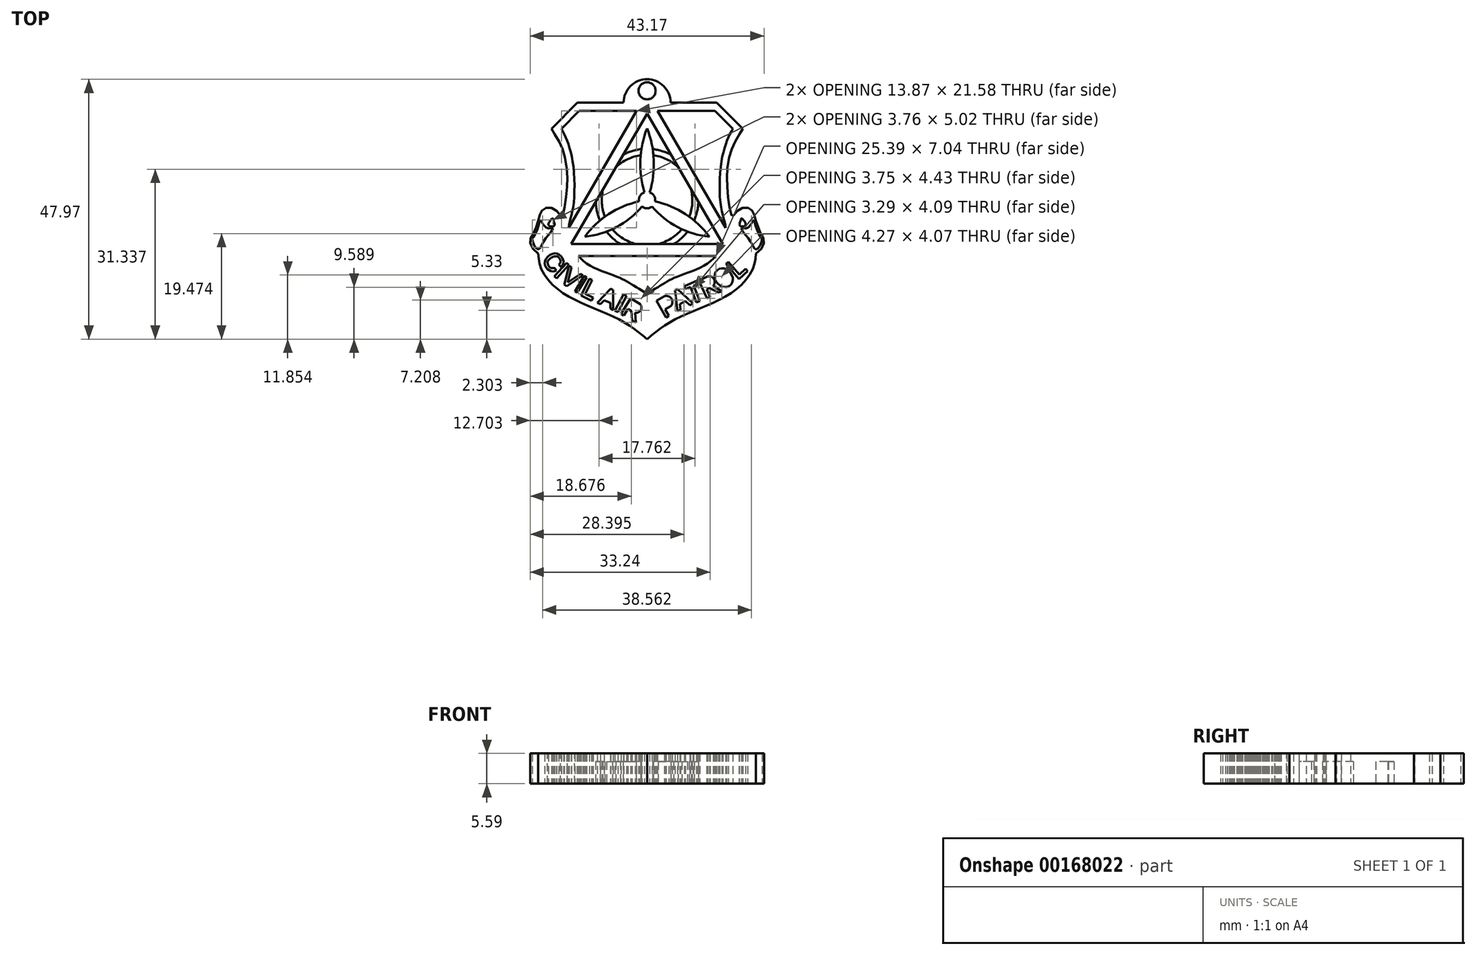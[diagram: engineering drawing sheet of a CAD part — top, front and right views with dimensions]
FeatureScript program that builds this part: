
annotation { "Feature Type Name" : "Feature", "Feature Type Description" : "" }
export const myFeature = defineFeature(function(context is Context, id is Id, definition is map)
    precondition{}
    {
        {
            var Q0;
            Q0=qCreatedBy(makeId("Top.planeOp"),FACE);
            var sketch = newSketch(context, id + "F0", { "sketchPlane" : qUnion([Q0])});
            skLineSegment(sketch, "E0", {"start": v(-6.93, 17.49) * mm, "end": v(-15.48, 17.49) * mm});
            skLineSegment(sketch, "E1", {"start": v(-15.48, 17.49) * mm, "end": v(-20.25, 12.66) * mm});
            skFitSpline(sketch, "E2", {"points": [v(-2.6, -26.15) * mm, v(-4.98, -24.26) * mm, v(-7.86, -22.47) * mm, v(-12.01, -20.64) * mm, v(-16.34, -18.68) * mm, v(-19.92, -16.22) * mm, v(-22.22, -12.94) * mm, v(-22.69, -10.37) * mm], "startDerivative": vector(-18.24, 15.04) * mm, "endDerivative": vector(-1.61, 21.12) * mm});
            skFitSpline(sketch, "E3", {"points": [v(-22.69, -10.37) * mm, v(-23.77, -9.4) * mm, v(-24.16, -8.34) * mm, v(-24.1, -7.52) * mm, v(-23.78, -7) * mm, v(-23.3, -6.01) * mm, v(-22.85, -4.85) * mm, v(-22.48, -3.49) * mm, v(-22.24, -2.77) * mm, v(-21.89, -2.3) * mm, v(-21.26, -1.9) * mm, v(-20.38, -1.88) * mm, v(-19.4, -2.36) * mm, v(-18.72, -3.08) * mm, v(-18.34, -3.62) * mm, v(-18.02, -2.67) * mm, v(-17.57, -0.25) * mm, v(-17.36, 2.67) * mm, v(-17.38, 5.12) * mm, v(-17.97, 8.14) * mm, v(-18.65, 9.93) * mm, v(-19.7, 11.76) * mm, v(-20.25, 12.66) * mm], "startDerivative": vector(-25.4, 18.97) * mm, "endDerivative": vector(-11.96, 19.7) * mm});
            skLineSegment(sketch, "E4", {"start": v(-2.6, 15.48) * mm, "end": v(-16.58, -8.6) * mm});
            skLineSegment(sketch, "E5", {"start": v(-16.58, -8.6) * mm, "end": v(-2.6, -8.6) * mm});
            skCircle(sketch, "E6", {"center": v(-2.6, -0.49) * mm, "radius": 1.51 * mm});
            skArc(sketch, "E7", {"start": v(-2.6, 12.77) * mm, "mid": v(-3.84, 6.9) * mm, "end": v(-3.1, 0.94) * mm});
            skArc(sketch, "E8", {"start": v(-4.09, -0.74) * mm, "mid": v(-9.7, -3.07) * mm, "end": v(-14.1, -7.25) * mm});
            skArc(sketch, "E9", {"start": v(-14.1, -7.25) * mm, "mid": v(-8.27, -5.49) * mm, "end": v(-3.52, -1.68) * mm});
            skLineSegment(sketch, "E10.trimOffspring", {"start": v(-2.6, -2) * mm, "end": v(-2.6, -27.2) * mm});
            skLineSegment(sketch, "E11", {"start": v(-4.54, 15.98) * mm, "end": v(-15.13, 15.98) * mm});
            skLineSegment(sketch, "E12", {"start": v(-15.13, 15.98) * mm, "end": v(-18.41, 12.66) * mm});
            skFitSpline(sketch, "E13", {"points": [v(-18.41, 12.66) * mm, v(-17.37, 10.48) * mm, v(-16.23, 5.97) * mm, v(-16.23, -1.7) * mm, v(-16.95, -4.73) * mm, v(-17.06, -6.85) * mm, v(-16.58, -8.6) * mm, v(-14.1, -11.94) * mm, v(-8.27, -14.6) * mm, v(-5.61, -15.92) * mm, v(-2.6, -17.81) * mm], "startDerivative": vector(13.13, -25.03) * mm, "endDerivative": vector(32.22, -20.65) * mm});
            skArc(sketch, "E14.MirrorCS", {"start": v(-2.6, 12.77) * mm, "mid": v(-1.35, 6.9) * mm, "end": v(-2.1, 0.94) * mm});
            skArc(sketch, "E15.MirrorCS", {"start": v(-1.1, -0.74) * mm, "mid": v(4.5, -3.07) * mm, "end": v(8.9, -7.25) * mm});
            skArc(sketch, "E16.MirrorCS", {"start": v(8.9, -7.25) * mm, "mid": v(3.07, -5.49) * mm, "end": v(-1.67, -1.68) * mm});
            skFitSpline(sketch, "E17.MirrorCS", {"points": [v(13.22, 12.66) * mm, v(12.18, 10.48) * mm, v(11.04, 5.97) * mm, v(11.04, -1.7) * mm, v(11.76, -4.73) * mm, v(11.87, -6.85) * mm, v(11.38, -8.6) * mm, v(8.91, -11.94) * mm, v(3.07, -14.6) * mm, v(0.42, -15.92) * mm, v(-2.6, -17.81) * mm], "startDerivative": vector(-13.13, -25.03) * mm, "endDerivative": vector(-32.22, -20.65) * mm});
            skFitSpline(sketch, "E18.MirrorCS", {"points": [v(-2.6, -26.15) * mm, v(-0.2, -24.26) * mm, v(2.66, -22.47) * mm, v(6.82, -20.64) * mm, v(11.14, -18.68) * mm, v(14.73, -16.22) * mm, v(17.02, -12.94) * mm, v(17.5, -10.37) * mm], "startDerivative": vector(18.24, 15.04) * mm, "endDerivative": vector(1.61, 21.12) * mm});
            skFitSpline(sketch, "E19.MirrorCS", {"points": [v(17.5, -10.37) * mm, v(18.57, -9.4) * mm, v(18.97, -8.34) * mm, v(18.91, -7.52) * mm, v(18.6, -7) * mm, v(18.1, -6.01) * mm, v(17.66, -4.85) * mm, v(17.28, -3.49) * mm, v(17.05, -2.77) * mm, v(16.7, -2.3) * mm, v(16.07, -1.9) * mm, v(15.19, -1.88) * mm, v(14.2, -2.36) * mm, v(13.53, -3.08) * mm, v(13.15, -3.62) * mm, v(12.83, -2.67) * mm, v(12.38, -0.25) * mm, v(12.16, 2.67) * mm, v(12.18, 5.12) * mm, v(12.77, 8.14) * mm, v(13.45, 9.93) * mm, v(14.5, 11.76) * mm, v(15.06, 12.66) * mm], "startDerivative": vector(25.4, 18.97) * mm, "endDerivative": vector(11.96, 19.7) * mm});
            skLineSegment(sketch, "E20.MirrorCS", {"start": v(9.94, 15.98) * mm, "end": v(13.22, 12.66) * mm});
            skLineSegment(sketch, "E21.MirrorCS", {"start": v(-0.65, 15.98) * mm, "end": v(9.94, 15.98) * mm});
            skLineSegment(sketch, "E22.MirrorCS", {"start": v(10.28, 17.49) * mm, "end": v(15.06, 12.66) * mm});
            skLineSegment(sketch, "E23.MirrorCS", {"start": v(1.74, 17.49) * mm, "end": v(10.28, 17.49) * mm});
            skLineSegment(sketch, "E24.MirrorCS", {"start": v(-2.6, 15.48) * mm, "end": v(11.38, -8.6) * mm});
            skLineSegment(sketch, "E25.MirrorCS", {"start": v(11.38, -8.6) * mm, "end": v(-2.6, -8.6) * mm});
            skArc(sketch, "E26", {"start": v(-12.07, -0.84) * mm, "mid": v(-11.84, -2.58) * mm, "end": v(-11.3, -4.26) * mm});
            skArc(sketch, "E27", {"start": v(-10.73, 1.47) * mm, "mid": v(-10.94, -1.07) * mm, "end": v(-10.38, -3.55) * mm});
            skArc(sketch, "E28.trimOffspring", {"start": v(2.3, -8.6) * mm, "mid": v(3.7, -7.57) * mm, "end": v(4.89, -6.3) * mm});
            skArc(sketch, "E29.trimOffspring", {"start": v(-0.56, -8.6) * mm, "mid": v(1.85, -7.57) * mm, "end": v(3.82, -5.86) * mm});
            skArc(sketch, "E30.trimOffspring", {"start": v(-9.01, -5.86) * mm, "mid": v(-7.04, -7.57) * mm, "end": v(-4.64, -8.6) * mm});
            skArc(sketch, "E31.trimOffspring", {"start": v(-10.08, -6.3) * mm, "mid": v(-8.9, -7.57) * mm, "end": v(-7.5, -8.6) * mm});
            skArc(sketch, "E32.trimOffspring", {"start": v(5.2, -3.55) * mm, "mid": v(5.75, -1.07) * mm, "end": v(5.54, 1.47) * mm});
            skArc(sketch, "E33.trimOffspring", {"start": v(6.1, -4.26) * mm, "mid": v(6.65, -2.58) * mm, "end": v(6.88, -0.84) * mm});
            skArc(sketch, "E34.trimOffspring", {"start": v(1.8, 7.91) * mm, "mid": v(0.17, 8.58) * mm, "end": v(-1.55, 8.94) * mm});
            skArc(sketch, "E35.trimOffspring", {"start": v(3.13, 5.61) * mm, "mid": v(1.03, 7.05) * mm, "end": v(-1.41, 7.8) * mm});
            skArc(sketch, "E36.trimOffspring", {"start": v(-3.64, 8.94) * mm, "mid": v(-5.36, 8.58) * mm, "end": v(-6.99, 7.91) * mm});
            skArc(sketch, "E37.trimOffspring", {"start": v(-3.78, 7.8) * mm, "mid": v(-6.22, 7.05) * mm, "end": v(-8.33, 5.61) * mm});
            skCircle(sketch, "E38", {"center": v(-2.6, 19.7) * mm, "radius": 1.59 * mm});
            skArc(sketch, "E39.trimOffspring", {"start": v(1.74, 17.49) * mm, "mid": v(-2.6, 21.82) * mm, "end": v(-6.93, 17.49) * mm});
            skLineSegment(sketch, "E40", {"start": v(-18.87, -12.4) * mm, "end": v(-18.42, -12.84) * mm});
            skLineSegment(sketch, "E41", {"start": v(-19.63, -13.02) * mm, "end": v(-19.36, -13.48) * mm});
            skFitSpline(sketch, "E42", {"points": [v(-19.36, -13.48) * mm, v(-20.24, -13.6) * mm, v(-21.25, -12.9) * mm, v(-21.42, -11.64) * mm, v(-19.94, -10.36) * mm, v(-18.6, -10.7) * mm, v(-18.03, -11.82) * mm, v(-18.42, -12.84) * mm], "startDerivative": vector(-7.77, -3.78) * mm, "endDerivative": vector(-5.66, -7.35) * mm});
            skFitSpline(sketch, "E43", {"points": [v(-19.63, -13.02) * mm, v(-20.29, -13.02) * mm, v(-20.76, -12.64) * mm, v(-20.96, -11.94) * mm, v(-20.5, -11.28) * mm, v(-19.63, -10.85) * mm, v(-18.9, -11.08) * mm, v(-18.56, -11.76) * mm, v(-18.87, -12.4) * mm], "startDerivative": vector(-5.37, -0.56) * mm, "endDerivative": vector(-3.77, -4.94) * mm});
            skLineSegment(sketch, "E44", {"start": v(-17.41, -12.1) * mm, "end": v(-17.04, -12.43) * mm});
            skLineSegment(sketch, "E45", {"start": v(-17.04, -12.43) * mm, "end": v(-19.26, -14.96) * mm});
            skLineSegment(sketch, "E46", {"start": v(-19.26, -14.96) * mm, "end": v(-19.7, -14.57) * mm});
            skLineSegment(sketch, "E47", {"start": v(-19.7, -14.57) * mm, "end": v(-17.41, -12.1) * mm});
            skLineSegment(sketch, "E48", {"start": v(-16.98, -12.6) * mm, "end": v(-16.54, -12.92) * mm});
            skLineSegment(sketch, "E49", {"start": v(-16.54, -12.92) * mm, "end": v(-17.26, -15.7) * mm});
            skLineSegment(sketch, "E50", {"start": v(-17.26, -15.7) * mm, "end": v(-14.91, -14.09) * mm});
            skLineSegment(sketch, "E51", {"start": v(-14.91, -14.09) * mm, "end": v(-14.45, -14.36) * mm});
            skLineSegment(sketch, "E52", {"start": v(-14.45, -14.36) * mm, "end": v(-17.41, -16.4) * mm});
            skLineSegment(sketch, "E53", {"start": v(-17.41, -16.4) * mm, "end": v(-17.86, -16.1) * mm});
            skLineSegment(sketch, "E54", {"start": v(-17.86, -16.1) * mm, "end": v(-16.98, -12.6) * mm});
            skLineSegment(sketch, "E55", {"start": v(-14.2, -14.44) * mm, "end": v(-13.74, -14.72) * mm});
            skLineSegment(sketch, "E56", {"start": v(-13.74, -14.72) * mm, "end": v(-15.5, -17.6) * mm});
            skLineSegment(sketch, "E57", {"start": v(-15.5, -17.6) * mm, "end": v(-15.92, -17.35) * mm});
            skLineSegment(sketch, "E58", {"start": v(-15.92, -17.35) * mm, "end": v(-14.2, -14.44) * mm});
            skLineSegment(sketch, "E59", {"start": v(-13.26, -15) * mm, "end": v(-12.72, -15.28) * mm});
            skLineSegment(sketch, "E60", {"start": v(-12.72, -15.28) * mm, "end": v(-13.98, -17.8) * mm});
            skLineSegment(sketch, "E61", {"start": v(-13.98, -17.8) * mm, "end": v(-12.55, -18.51) * mm});
            skLineSegment(sketch, "E62", {"start": v(-12.55, -18.51) * mm, "end": v(-12.83, -19.08) * mm});
            skLineSegment(sketch, "E63", {"start": v(-12.83, -19.08) * mm, "end": v(-14.8, -18.1) * mm});
            skLineSegment(sketch, "E64", {"start": v(-14.8, -18.1) * mm, "end": v(-13.26, -15) * mm});
            skLineSegment(sketch, "E65", {"start": v(-9.28, -16.86) * mm, "end": v(-11.77, -19.43) * mm});
            skLineSegment(sketch, "E66", {"start": v(-11.77, -19.43) * mm, "end": v(-11.18, -19.73) * mm});
            skLineSegment(sketch, "E67", {"start": v(-11.18, -19.73) * mm, "end": v(-10.53, -18.98) * mm});
            skLineSegment(sketch, "E68", {"start": v(-10.53, -18.98) * mm, "end": v(-9.36, -19.42) * mm});
            skLineSegment(sketch, "E69", {"start": v(-9.36, -19.42) * mm, "end": v(-9.36, -20.49) * mm});
            skLineSegment(sketch, "E70", {"start": v(-9.36, -20.49) * mm, "end": v(-8.83, -20.75) * mm});
            skLineSegment(sketch, "E71", {"start": v(-8.83, -20.75) * mm, "end": v(-8.83, -17.12) * mm});
            skLineSegment(sketch, "E72", {"start": v(-8.83, -17.12) * mm, "end": v(-9.28, -16.86) * mm});
            skLineSegment(sketch, "E73", {"start": v(-9.28, -17.61) * mm, "end": v(-10.13, -18.54) * mm});
            skLineSegment(sketch, "E74", {"start": v(-10.13, -18.54) * mm, "end": v(-9.28, -18.85) * mm});
            skLineSegment(sketch, "E75", {"start": v(-9.28, -18.85) * mm, "end": v(-9.28, -17.61) * mm});
            skLineSegment(sketch, "E76", {"start": v(-6.94, -17.91) * mm, "end": v(-6.4, -18.18) * mm});
            skLineSegment(sketch, "E77", {"start": v(-6.4, -18.18) * mm, "end": v(-8, -21.16) * mm});
            skLineSegment(sketch, "E78", {"start": v(-8, -21.16) * mm, "end": v(-8.54, -20.89) * mm});
            skLineSegment(sketch, "E79", {"start": v(-8.54, -20.89) * mm, "end": v(-6.94, -17.91) * mm});
            skLineSegment(sketch, "E80", {"start": v(-5.63, -18.6) * mm, "end": v(-7.38, -21.47) * mm});
            skLineSegment(sketch, "E81", {"start": v(-7.38, -21.47) * mm, "end": v(-6.88, -21.77) * mm});
            skLineSegment(sketch, "E82", {"start": v(-6.88, -21.77) * mm, "end": v(-6.15, -20.57) * mm});
            skLineSegment(sketch, "E83", {"start": v(-6.15, -20.57) * mm, "end": v(-5.5, -20.96) * mm});
            skLineSegment(sketch, "E84", {"start": v(-5.5, -20.96) * mm, "end": v(-5.36, -22.7) * mm});
            skLineSegment(sketch, "E85", {"start": v(-5.36, -22.7) * mm, "end": v(-4.67, -23.04) * mm});
            skLineSegment(sketch, "E86", {"start": v(-4.67, -23.04) * mm, "end": v(-4.83, -21.26) * mm});
            skLineSegment(sketch, "E87", {"start": v(-5.63, -18.6) * mm, "end": v(-3.87, -19.68) * mm});
            skArc(sketch, "E88", {"start": v(-4.83, -21.26) * mm, "mid": v(-3.76, -20.83) * mm, "end": v(-3.87, -19.68) * mm});
            skArc(sketch, "E89", {"start": v(-4.89, -20.7) * mm, "mid": v(-4.27, -20.54) * mm, "end": v(-4.44, -19.92) * mm});
            skLineSegment(sketch, "E90", {"start": v(-4.44, -19.92) * mm, "end": v(-5.44, -19.37) * mm});
            skLineSegment(sketch, "E91", {"start": v(-5.44, -19.37) * mm, "end": v(-5.84, -20.1) * mm});
            skLineSegment(sketch, "E92", {"start": v(-5.84, -20.1) * mm, "end": v(-4.89, -20.7) * mm});
            skLineSegment(sketch, "E93", {"start": v(0.91, -22.15) * mm, "end": v(-0.85, -19.05) * mm});
            skLineSegment(sketch, "E94", {"start": v(-0.85, -19.05) * mm, "end": v(0.62, -18.22) * mm});
            skLineSegment(sketch, "E95", {"start": v(0.91, -22.15) * mm, "end": v(1.4, -21.87) * mm});
            skLineSegment(sketch, "E96", {"start": v(1.4, -21.87) * mm, "end": v(0.73, -20.68) * mm});
            skLineSegment(sketch, "E97", {"start": v(0.73, -20.68) * mm, "end": v(1.77, -20.09) * mm});
            skLineSegment(sketch, "E98", {"start": v(-0.1, -19.25) * mm, "end": v(0.46, -20.21) * mm});
            skLineSegment(sketch, "E99", {"start": v(0.46, -20.21) * mm, "end": v(1.25, -19.75) * mm});
            skLineSegment(sketch, "E100", {"start": v(-0.1, -19.25) * mm, "end": v(0.65, -18.82) * mm});
            skLineSegment(sketch, "E101", {"start": v(2.57, -17.13) * mm, "end": v(3.03, -20.99) * mm});
            skLineSegment(sketch, "E102", {"start": v(3.03, -20.99) * mm, "end": v(3.6, -20.7) * mm});
            skLineSegment(sketch, "E103", {"start": v(3.6, -20.7) * mm, "end": v(3.44, -19.67) * mm});
            skLineSegment(sketch, "E104", {"start": v(3.44, -19.67) * mm, "end": v(4.5, -19.1) * mm});
            skLineSegment(sketch, "E105", {"start": v(4.5, -19.1) * mm, "end": v(5.3, -19.88) * mm});
            skLineSegment(sketch, "E106", {"start": v(5.3, -19.88) * mm, "end": v(5.86, -19.56) * mm});
            skLineSegment(sketch, "E107", {"start": v(5.86, -19.56) * mm, "end": v(3.01, -16.9) * mm});
            skLineSegment(sketch, "E108", {"start": v(3.01, -16.9) * mm, "end": v(2.57, -17.13) * mm});
            skLineSegment(sketch, "E109", {"start": v(3.14, -17.72) * mm, "end": v(3.32, -19.11) * mm});
            skLineSegment(sketch, "E110", {"start": v(3.32, -19.11) * mm, "end": v(4.13, -18.68) * mm});
            skLineSegment(sketch, "E111", {"start": v(4.13, -18.68) * mm, "end": v(3.14, -17.72) * mm});
            skLineSegment(sketch, "E112", {"start": v(4.27, -16.42) * mm, "end": v(4.46, -16.9) * mm});
            skLineSegment(sketch, "E113", {"start": v(4.46, -16.9) * mm, "end": v(5.4, -16.53) * mm});
            skLineSegment(sketch, "E114", {"start": v(5.4, -16.53) * mm, "end": v(6.52, -19.36) * mm});
            skLineSegment(sketch, "E115", {"start": v(6.52, -19.36) * mm, "end": v(7.14, -19.11) * mm});
            skLineSegment(sketch, "E116", {"start": v(7.14, -19.11) * mm, "end": v(6.03, -16.29) * mm});
            skLineSegment(sketch, "E117", {"start": v(6.03, -16.29) * mm, "end": v(6.94, -15.93) * mm});
            skLineSegment(sketch, "E118", {"start": v(6.94, -15.93) * mm, "end": v(6.7, -15.34) * mm});
            skLineSegment(sketch, "E119", {"start": v(6.7, -15.34) * mm, "end": v(4.27, -16.42) * mm});
            skLineSegment(sketch, "E120", {"start": v(6.92, -15.35) * mm, "end": v(8.47, -18.6) * mm});
            skLineSegment(sketch, "E121", {"start": v(8.47, -18.6) * mm, "end": v(9.04, -18.34) * mm});
            skLineSegment(sketch, "E122", {"start": v(9.04, -18.34) * mm, "end": v(8.41, -16.94) * mm});
            skLineSegment(sketch, "E123", {"start": v(8.41, -16.94) * mm, "end": v(8.93, -16.71) * mm});
            skLineSegment(sketch, "E124", {"start": v(8.93, -16.71) * mm, "end": v(10.58, -17.57) * mm});
            skLineSegment(sketch, "E125", {"start": v(10.58, -17.57) * mm, "end": v(11.2, -17.33) * mm});
            skLineSegment(sketch, "E126", {"start": v(6.92, -15.35) * mm, "end": v(8.6, -14.56) * mm});
            skLineSegment(sketch, "E127", {"start": v(7.63, -15.54) * mm, "end": v(8.1, -16.47) * mm});
            skLineSegment(sketch, "E128", {"start": v(8.1, -16.47) * mm, "end": v(9.19, -15.92) * mm});
            skLineSegment(sketch, "E129", {"start": v(7.63, -15.54) * mm, "end": v(8.63, -15.04) * mm});
            skLineSegment(sketch, "E130", {"start": v(11.2, -17.33) * mm, "end": v(9.6, -16.3) * mm});
            skArc(sketch, "E131", {"start": v(1.77, -20.09) * mm, "mid": v(1.92, -18.7) * mm, "end": v(0.62, -18.22) * mm});
            skArc(sketch, "E132", {"start": v(1.25, -19.75) * mm, "mid": v(1.4, -19) * mm, "end": v(0.65, -18.82) * mm});
            skArc(sketch, "E133", {"start": v(9.6, -16.3) * mm, "mid": v(9.76, -15.05) * mm, "end": v(8.6, -14.56) * mm});
            skArc(sketch, "E134", {"start": v(9.19, -15.92) * mm, "mid": v(9.3, -15.22) * mm, "end": v(8.63, -15.04) * mm});
            skEllipse(sketch, "E135", {"center": v(11.56, -14.8) * mm, "majorRadius": 1.32 * mm, "minorRadius": 1.03 * mm, "majorAxis": v(-0.63, 0.78)});
            skEllipse(sketch, "E136", {"center": v(11.56, -14.8) * mm, "majorRadius": 1.85 * mm, "minorRadius": 1.55 * mm, "majorAxis": v(-0.64, 0.77)});
            skLineSegment(sketch, "E137", {"start": v(11.97, -12.3) * mm, "end": v(14.4, -15.04) * mm});
            skLineSegment(sketch, "E138", {"start": v(14.4, -15.04) * mm, "end": v(16, -13.62) * mm});
            skLineSegment(sketch, "E139", {"start": v(16, -13.62) * mm, "end": v(15.6, -13.18) * mm});
            skLineSegment(sketch, "E140", {"start": v(15.6, -13.18) * mm, "end": v(14.42, -14.21) * mm});
            skLineSegment(sketch, "E141", {"start": v(14.42, -14.21) * mm, "end": v(12.43, -11.91) * mm});
            skLineSegment(sketch, "E142", {"start": v(12.43, -11.91) * mm, "end": v(11.97, -12.3) * mm});
            skFitSpline(sketch, "E143", {"points": [v(-19.84, -4.37) * mm, v(-19.75, -5.23) * mm, v(-20.78, -5.08) * mm, v(-20.04, -3.87) * mm, v(-19.84, -4.37) * mm]});
            skFitSpline(sketch, "E144.MirrorC", {"points": [v(14.65, -4.37) * mm, v(14.56, -5.23) * mm, v(15.6, -5.08) * mm, v(14.85, -3.87) * mm, v(14.65, -4.37) * mm]});
            skFitSpline(sketch, "E145", {"points": [v(17.1, -4.16) * mm, v(16.48, -5.11) * mm, v(15.53, -5.7) * mm, v(14.81, -5.7) * mm, v(15.57, -6.9) * mm, v(16.7, -8.47) * mm, v(17.41, -9.57) * mm, v(18.11, -9.11) * mm, v(18.6, -7.62) * mm, v(18.34, -7.27) * mm, v(17.43, -5.17) * mm, v(17.1, -4.16) * mm]});
            skFitSpline(sketch, "E146.MirrorC", {"points": [v(-22.3, -4.16) * mm, v(-21.67, -5.11) * mm, v(-20.73, -5.7) * mm, v(-20, -5.7) * mm, v(-20.76, -6.9) * mm, v(-21.9, -8.47) * mm, v(-22.6, -9.57) * mm, v(-23.3, -9.11) * mm, v(-23.8, -7.62) * mm, v(-23.53, -7.27) * mm, v(-22.62, -5.17) * mm, v(-22.3, -4.16) * mm]});
            skLineSegment(sketch, "E147", {"start": v(-4.54, 15.98) * mm, "end": v(-17.07, -5.6) * mm});
            skLineSegment(sketch, "E148", {"start": v(-15.29, -10.78) * mm, "end": v(10.1, -10.78) * mm});
            skLineSegment(sketch, "E149.MirrorCS", {"start": v(-0.65, 15.98) * mm, "end": v(11.88, -5.6) * mm});
            skPoint(sketch, "E150.start.orphan", {"position": v(-3.55, 15.48) * mm});
            skSolve(sketch);
        }
        {
            var Q0;
            Q0=makeQuery(id+"F0.imprint","IMPRINT",FACE,{"disambiguationData":[TD([[makeQuery(id+"F0.imprint","IMPRINT",EDGE,{"derivedFrom":sQuery(id+"F0.wireOp",EDGE,"E0")}),1.0]])]});
            var Q1;
            Q1=makeQuery(id+"F0.imprint","IMPRINT",FACE,{"disambiguationData":[TD([[makeQuery(id+"F0.imprint","IMPRINT",EDGE,{"derivedFrom":sQuery(id+"F0.wireOp",EDGE,"E0")}),1.0]])]});
            var Q2;
            {var subQ0=sQuery(id+"F0.wireOp",EDGE,"E6");var subQ6=makeQuery(id+"F0.imprint","INTERSECT",VERTEX,{"derivedFrom":[subQ0,sQuery(id+"F0.wireOp",EDGE,"E7")]});Q2=makeQuery(id+"F0.imprint","IMPRINT",FACE,{"disambiguationData":[TD([[makeQuery(id+"F0.imprint","IMPRINT",EDGE,{"disambiguationData":[TD([[subQ6,1.0]])],"derivedFrom":subQ0}),1.0]])]});}
            var Q3;
            {var subQ1=sQuery(id+"F0.wireOp",EDGE,"E8");var subQ5=sQuery(id+"F0.wireOp",EDGE,"E6");var subQ6=makeQuery(id+"F0.imprint","INTERSECT",VERTEX,{"derivedFrom":[subQ5,subQ1]});Q3=makeQuery(id+"F0.imprint","IMPRINT",FACE,{"disambiguationData":[TD([[makeQuery(id+"F0.imprint","IMPRINT",EDGE,{"disambiguationData":[TD([[subQ6,-1.0]])],"derivedFrom":subQ5}),-1.0]])]});}
            var Q4;
            {var subQ1=sQuery(id+"F0.wireOp",EDGE,"E15.MirrorCS");var subQ5=sQuery(id+"F0.wireOp",EDGE,"E6");var subQ6=makeQuery(id+"F0.imprint","INTERSECT",VERTEX,{"derivedFrom":[subQ5,subQ1]});Q4=makeQuery(id+"F0.imprint","IMPRINT",FACE,{"disambiguationData":[TD([[makeQuery(id+"F0.imprint","IMPRINT",EDGE,{"disambiguationData":[TD([[subQ6,1.0]])],"derivedFrom":subQ5}),-1.0]])]});}
            var Q5;
            {var subQ0=sQuery(id+"F0.wireOp",EDGE,"E7");var subQ1=sQuery(id+"F0.wireOp",EDGE,"E6");var subQ2=makeQuery(id+"F0.imprint","INTERSECT",VERTEX,{"derivedFrom":[subQ1,subQ0]});Q5=makeQuery(id+"F0.imprint","IMPRINT",FACE,{"disambiguationData":[TD([[makeQuery(id+"F0.imprint","IMPRINT",EDGE,{"disambiguationData":[TD([[subQ2,1.0]])],"derivedFrom":subQ1}),-1.0]])]});}
            var Q6;
            {var subQ16=sQuery(id+"F0.wireOp",EDGE,"dyDLpNgW-xe3w-nZMA-enaF-uUpdJC2aTEYf");Q6=makeQuery(id+"F0.imprint","IMPRINT",FACE,{"disambiguationData":[TD([[makeQuery(id+"F0.imprint","IMPRINT",EDGE,{"derivedFrom":subQ16}),1.0]])]});}
            var Q7;
            {var subQ1=sQuery(id+"F0.wireOp",EDGE,"E5");var subQ8=makeQuery(id+"F0.imprint","INTERSECT",VERTEX,{"derivedFrom":[subQ1,sQuery(id+"F0.wireOp",EDGE,"E30.trimOffspring")]});Q7=makeQuery(id+"F0.imprint","IMPRINT",FACE,{"disambiguationData":[TD([[makeQuery(id+"F0.imprint","IMPRINT",EDGE,{"disambiguationData":[TD([[subQ8,1.0]])],"derivedFrom":subQ1}),-1.0]])]});}
            var Q8;
            {var subQ0=sQuery(id+"F0.wireOp",EDGE,"E25.MirrorCS");var subQ3=makeQuery(id+"F0.imprint","INTERSECT",VERTEX,{"derivedFrom":[subQ0,sQuery(id+"F0.wireOp",EDGE,"E28.trimOffspring")]});Q8=makeQuery(id+"F0.imprint","IMPRINT",FACE,{"disambiguationData":[TD([[makeQuery(id+"F0.imprint","IMPRINT",EDGE,{"disambiguationData":[TD([[subQ3,-1.0]])],"derivedFrom":subQ0}),1.0]])]});}
            var Q9;
            {var subQ9=sQuery(id+"F0.wireOp",EDGE,"E150");Q9=makeQuery(id+"F0.imprint","IMPRINT",FACE,{"disambiguationData":[TD([[makeQuery(id+"F0.imprint","IMPRINT",EDGE,{"derivedFrom":subQ9}),-1.0]])]});}
            var Q10;
            {var subQ3=sQuery(id+"F0.wireOp",EDGE,"762fb76b-fc70-4e15-b9cc-5fbb3dd3ec3d.trimOffspring");Q10=makeQuery(id+"F0.imprint","IMPRINT",FACE,{"disambiguationData":[TD([[makeQuery(id+"F0.imprint","IMPRINT",EDGE,{"derivedFrom":subQ3}),-1.0]])]});}
            extrude(context, id + "F1", {"entities" : qUnion([Q0, Q1, Q2, Q3, Q4, Q5, Q6, Q7, Q8, Q9, Q10]), "depth" : 5.6 * mm});
        }
        {
            var Q0;
            {var subQ0=sQuery(id+"F0.wireOp",EDGE,"E36.trimOffspring");Q0=makeQuery(id+"F0.imprint","IMPRINT",FACE,{"disambiguationData":[TD([[makeQuery(id+"F0.imprint","IMPRINT",EDGE,{"derivedFrom":subQ0}),1.0]])]});}
            var Q1;
            {var subQ0=sQuery(id+"F0.wireOp",EDGE,"E34.trimOffspring");Q1=makeQuery(id+"F0.imprint","IMPRINT",FACE,{"disambiguationData":[TD([[makeQuery(id+"F0.imprint","IMPRINT",EDGE,{"derivedFrom":subQ0}),1.0]])]});}
            var Q2;
            {var subQ0=sQuery(id+"F0.wireOp",EDGE,"E32.trimOffspring");Q2=makeQuery(id+"F0.imprint","IMPRINT",FACE,{"disambiguationData":[TD([[makeQuery(id+"F0.imprint","IMPRINT",EDGE,{"derivedFrom":subQ0}),-1.0]])]});}
            var Q3;
            {var subQ0=sQuery(id+"F0.wireOp",EDGE,"E28.trimOffspring");Q3=makeQuery(id+"F0.imprint","IMPRINT",FACE,{"disambiguationData":[TD([[makeQuery(id+"F0.imprint","IMPRINT",EDGE,{"derivedFrom":subQ0}),1.0]])]});}
            var Q4;
            {var subQ0=sQuery(id+"F0.wireOp",EDGE,"E30.trimOffspring");Q4=makeQuery(id+"F0.imprint","IMPRINT",FACE,{"disambiguationData":[TD([[makeQuery(id+"F0.imprint","IMPRINT",EDGE,{"derivedFrom":subQ0}),-1.0]])]});}
            var Q5;
            {var subQ0=sQuery(id+"F0.wireOp",EDGE,"E26");Q5=makeQuery(id+"F0.imprint","IMPRINT",FACE,{"disambiguationData":[TD([[makeQuery(id+"F0.imprint","IMPRINT",EDGE,{"derivedFrom":subQ0}),1.0]])]});}
            extrude(context, id + "F2", {"entities" : qUnion([Q0, Q1, Q2, Q3, Q4, Q5]), "operationType" : NewBodyOperationType.ADD, "depth" : 4.06 * mm});
        }
        {
            var Q0;
            Q0=makeQuery(id+"F0.imprint","IMPRINT",FACE,{"disambiguationData":[TD([[makeQuery(id+"F0.imprint","IMPRINT",EDGE,{"derivedFrom":sQuery(id+"F0.wireOp",EDGE,"E38")}),-1.0]])]});
            extrude(context, id + "F3", {"entities" : qUnion([Q0]), "operationType" : NewBodyOperationType.ADD, "depth" : 3.17 * mm});
        }
    });
